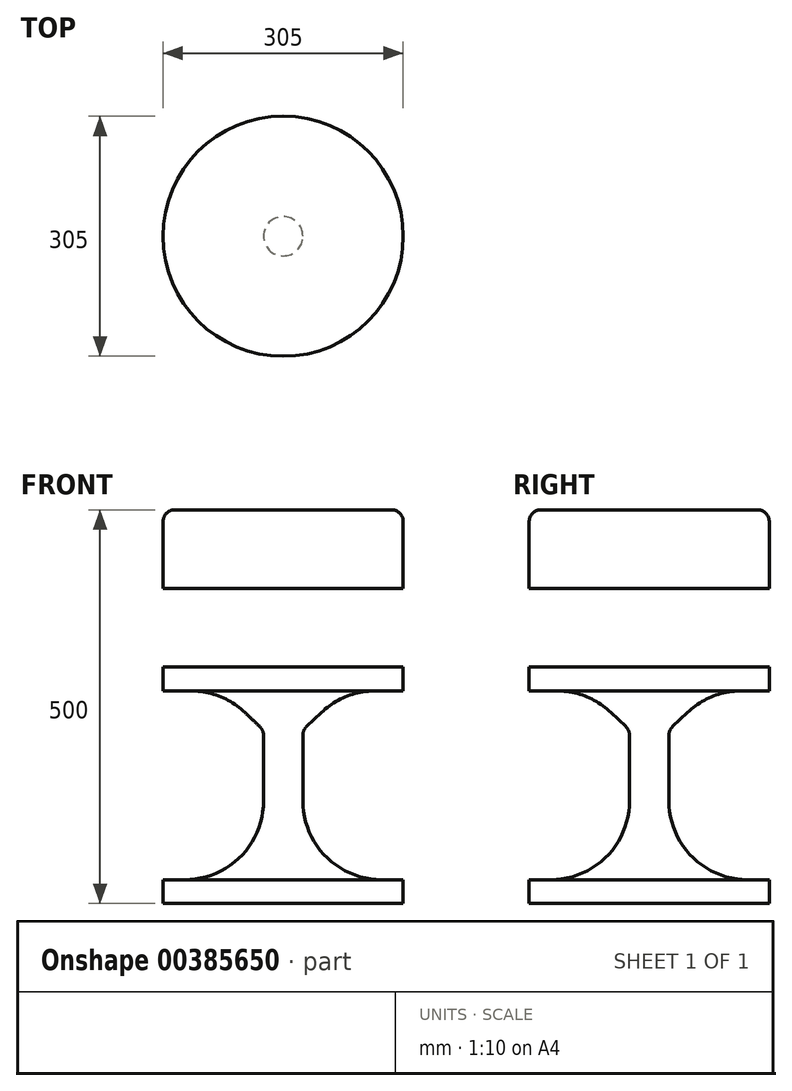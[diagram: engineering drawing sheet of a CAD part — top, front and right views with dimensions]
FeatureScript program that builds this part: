
annotation { "Feature Type Name" : "Feature", "Feature Type Description" : "" }
export const myFeature = defineFeature(function(context is Context, id is Id, definition is map)
    precondition{}
    {
        {
            var Q0;
            Q0=qCreatedBy(makeId("Front.planeOp"),FACE);
            var sketch = newSketch(context, id + "F0", { "sketchPlane" : qUnion([Q0])});
            skLineSegment(sketch, "E0.bottom", {"start": v(0, 0) * mm, "end": v(152.5, 0) * mm});
            skLineSegment(sketch, "E0.top", {"start": v(0, 300) * mm, "end": v(152.5, 300) * mm});
            skLineSegment(sketch, "E0.left", {"start": v(0, 0) * mm, "end": v(0, 300) * mm});
            skLineSegment(sketch, "E0.right", {"start": v(152.5, 0) * mm, "end": v(152.5, 30) * mm});
            skLineSegment(sketch, "E1.bottom", {"start": v(0, 400) * mm, "end": v(152.5, 400) * mm});
            skLineSegment(sketch, "E1.top", {"start": v(0, 500) * mm, "end": v(152.5, 500) * mm});
            skLineSegment(sketch, "E1.left", {"start": v(0, 400) * mm, "end": v(0, 500) * mm});
            skLineSegment(sketch, "E1.right", {"start": v(152.5, 400) * mm, "end": v(152.5, 500) * mm});
            skLineSegment(sketch, "E2", {"start": v(152.5, 270) * mm, "end": v(117.5, 270) * mm});
            skLineSegment(sketch, "E3", {"start": v(25, 213.57) * mm, "end": v(25, 130) * mm});
            skLineSegment(sketch, "E4", {"start": v(125, 30) * mm, "end": v(152.5, 30) * mm});
            skLineSegment(sketch, "E5.trimOffspring", {"start": v(152.5, 270) * mm, "end": v(152.5, 300) * mm});
            skLineSegment(sketch, "E6", {"start": v(48.53, 242.41) * mm, "end": v(29.66, 224.43) * mm});
            skPoint(sketch, "E7.visualSharp", {"position": v(25, 30) * mm});
            skArc(sketch, "E7.filletArc", {"start": v(25, 130) * mm, "mid": v(54.29, 59.29) * mm, "end": v(125, 30) * mm});
            skPoint(sketch, "E8.visualSharp", {"position": v(25, 220) * mm});
            skArc(sketch, "E8.filletArc", {"start": v(29.66, 224.43) * mm, "mid": v(26.21, 219.48) * mm, "end": v(25, 213.57) * mm});
            skPoint(sketch, "E9.visualSharp", {"position": v(77.5, 270) * mm});
            skArc(sketch, "E9.filletArc", {"start": v(117.5, 270) * mm, "mid": v(80.36, 262.85) * mm, "end": v(48.53, 242.41) * mm});
            skSolve(sketch);
        }
        {
            var Q0;
            Q0 = qSketchRegion(id + "F0", true);
            var Q1;
            Q1=sQuery(id+"F0.wireOp",EDGE,"E0.left");
            revolve(context, id + "F1", {"entities" : qUnion([Q0]), "axis" : qUnion([Q1]), "revolveType" : RevolveType.FULL});
        }
        {
            var Q0;
            Q0=makeQuery(id+"F1.opRevolve","SWEPT_EDGE",EDGE,{"disambiguationData":[OSD([sQuery(id+"F0.wireOp",EDGE,"E1.top"),sQuery(id+"F0.wireOp",EDGE,"E1.right")])]});
            fillet(context, id + "F2", {"entities" : qUnion([Q0]), "radius" : 15 * mm, "tangentPropagation" : true, "allowEdgeOverflow" : false});
        }
    });
